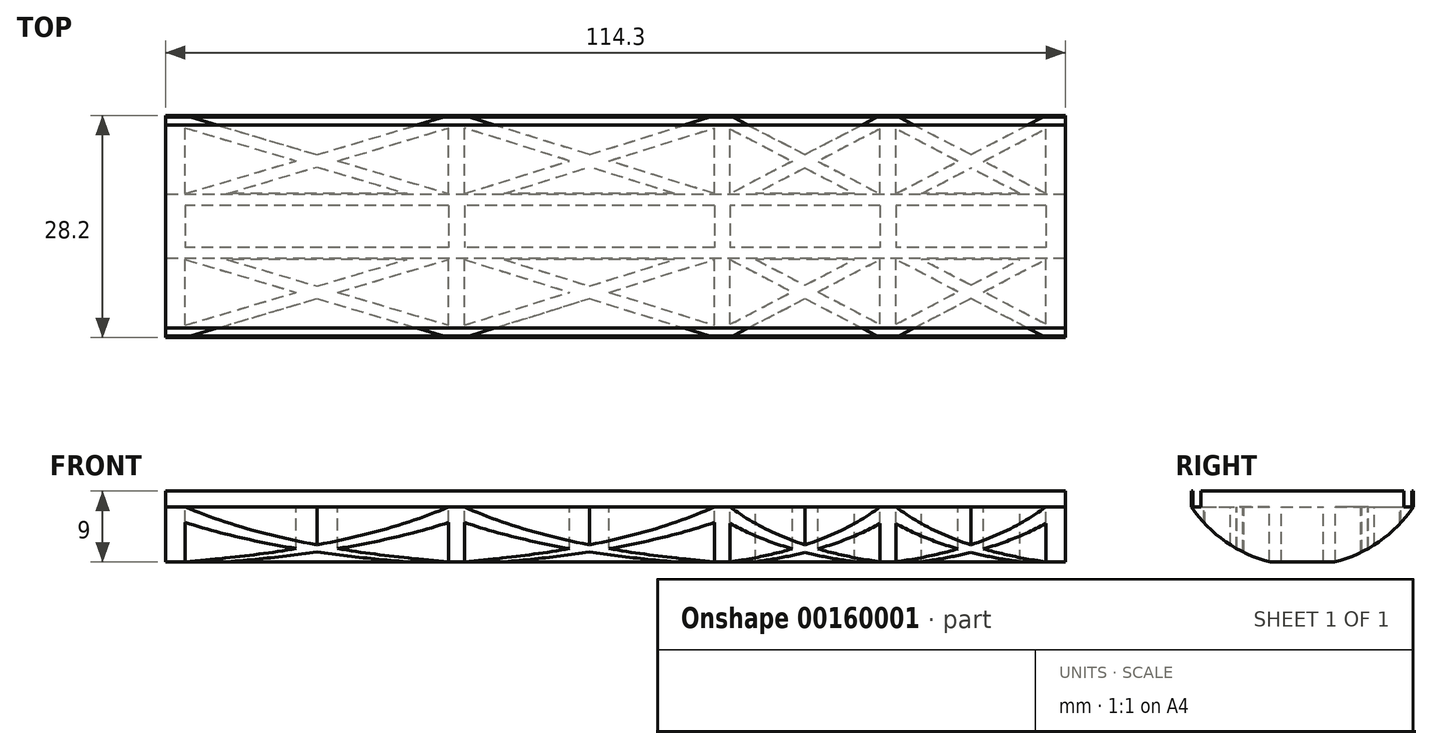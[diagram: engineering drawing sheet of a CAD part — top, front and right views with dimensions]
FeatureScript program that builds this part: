
annotation { "Feature Type Name" : "Feature", "Feature Type Description" : "" }
export const myFeature = defineFeature(function(context is Context, id is Id, definition is map)
    precondition{}
    {
        {
            var Q0;
            Q0=qCreatedBy(makeId("Right.planeOp"),FACE);
            var sketch = newSketch(context, id + "F0", { "sketchPlane" : qUnion([Q0])});
            skArc(sketch, "E0", {"start": v(-14.1, -9.5) * mm, "mid": v(0, -17) * mm, "end": v(14.1, -9.5) * mm});
            skLineSegment(sketch, "E1", {"start": v(-14.1, -9.5) * mm, "end": v(14.1, -9.5) * mm});
            skLineSegment(sketch, "E2", {"start": v(-12.9, -9.5) * mm, "end": v(-12.9, -7.5) * mm});
            skLineSegment(sketch, "E3", {"start": v(-12.9, -7.5) * mm, "end": v(12.9, -7.5) * mm});
            skLineSegment(sketch, "E4", {"start": v(12.9, -7.5) * mm, "end": v(12.9, -9.5) * mm});
            skSolve(sketch);
        }
        {
            var Q0;
            Q0=sQuery(id+"F0.wireOp",EDGE,"E1");
            cPlane(context, id + "F1", {"entities" : qUnion([Q0]), "cplaneType" : CPlaneType.LINE_ANGLE, "offset" : 25.4 * mm, "angle" : 0 * degree, "width" : 152.4 * mm, "height" : 152.4 * mm});
        }
        {
            var Q0;
            Q0 = qSketchRegion(id + "F0", true);
            extrude(context, id + "F2", {"entities" : qUnion([Q0]), "endBound" : BoundingType.SYMMETRIC, "depth" : 114.3 * mm});
        }
        {
            var Q0;
            Q0=qCreatedBy(id+"F1.planeOp",FACE);
            var sketch = newSketch(context, id + "F3", { "sketchPlane" : qUnion([Q0])});
            skLineSegment(sketch, "E5.top", {"start": v(-57.15, 14.1) * mm, "end": v(-54.65, 14.1) * mm});
            skLineSegment(sketch, "E5.left", {"start": v(-57.15, -14.1) * mm, "end": v(-57.15, 14.1) * mm});
            skLineSegment(sketch, "E5.right", {"start": v(57.15, -14.1) * mm, "end": v(57.15, 14.1) * mm});
            skLineSegment(sketch, "E6", {"start": v(-57.15, -14.1) * mm, "end": v(-54.65, -14.1) * mm});
            skLineSegment(sketch, "E7", {"start": v(-54.65, -12.53) * mm, "end": v(-54.65, -4.17) * mm});
            skLineSegment(sketch, "E8", {"start": v(54.65, -12.4) * mm, "end": v(54.65, -4.17) * mm});
            skLineSegment(sketch, "E9", {"start": v(35.6, -12.4) * mm, "end": v(35.6, -4.17) * mm});
            skLineSegment(sketch, "E10", {"start": v(33.6, -12.4) * mm, "end": v(33.6, -4.18) * mm});
            skLineSegment(sketch, "E11", {"start": v(14.55, -12.4) * mm, "end": v(14.55, -4.17) * mm});
            skLineSegment(sketch, "E12", {"start": v(12.55, -12.53) * mm, "end": v(12.55, -4.17) * mm});
            skLineSegment(sketch, "E13", {"start": v(-21.2, -12.53) * mm, "end": v(-21.2, -4.17) * mm});
            skLineSegment(sketch, "E14", {"start": v(-19.2, -12.53) * mm, "end": v(-19.2, -4.17) * mm});
            skLineSegment(sketch, "E15", {"start": v(-54.65, -2.68) * mm, "end": v(-21.2, -2.68) * mm});
            skLineSegment(sketch, "E16", {"start": v(-54.65, 2.68) * mm, "end": v(-21.2, 2.68) * mm});
            skLineSegment(sketch, "E17", {"start": v(-49.38, -4.17) * mm, "end": v(-26.47, -4.17) * mm});
            skLineSegment(sketch, "E18", {"start": v(-49.38, 4.17) * mm, "end": v(-26.47, 4.17) * mm});
            skLineSegment(sketch, "E19", {"start": v(-54.65, -14.1) * mm, "end": v(-37.92, -9.14) * mm});
            skLineSegment(sketch, "E20", {"start": v(-54.65, -4.17) * mm, "end": v(-40.56, -8.35) * mm});
            skLineSegment(sketch, "E21", {"start": v(-19.2, -14.1) * mm, "end": v(-3.32, -9.14) * mm});
            skLineSegment(sketch, "E22", {"start": v(-19.2, -4.18) * mm, "end": v(-5.84, -8.35) * mm});
            skLineSegment(sketch, "E23", {"start": v(14.55, -14.1) * mm, "end": v(24.08, -9.14) * mm});
            skLineSegment(sketch, "E24", {"start": v(14.55, -4.17) * mm, "end": v(22.45, -8.3) * mm});
            skLineSegment(sketch, "E25", {"start": v(35.6, -14.1) * mm, "end": v(45.13, -9.14) * mm});
            skLineSegment(sketch, "E26", {"start": v(54.65, -14.1) * mm, "end": v(45.13, -9.14) * mm});
            skLineSegment(sketch, "E27", {"start": v(-54.65, 14.1) * mm, "end": v(-37.92, 9.14) * mm});
            skLineSegment(sketch, "E28", {"start": v(-19.2, 4.17) * mm, "end": v(-5.84, 8.35) * mm});
            skLineSegment(sketch, "E29", {"start": v(14.55, 14.1) * mm, "end": v(24.08, 9.14) * mm});
            skLineSegment(sketch, "E30", {"start": v(35.6, 4.17) * mm, "end": v(43.5, 8.3) * mm});
            skLineSegment(sketch, "E31", {"start": v(54.65, 4.17) * mm, "end": v(46.75, 8.3) * mm});
            skLineSegment(sketch, "E32", {"start": v(33.6, 14.1) * mm, "end": v(24.08, 9.14) * mm});
            skLineSegment(sketch, "E33", {"start": v(12.55, 4.17) * mm, "end": v(-0.81, 8.35) * mm});
            skLineSegment(sketch, "E34", {"start": v(-54.65, 4.18) * mm, "end": v(-40.56, 8.35) * mm});
            skLineSegment(sketch, "E35.trimOffspring", {"start": v(-21.2, -14.1) * mm, "end": v(-19.2, -14.1) * mm});
            skLineSegment(sketch, "E36.trimOffspring", {"start": v(12.55, -14.1) * mm, "end": v(14.55, -14.1) * mm});
            skLineSegment(sketch, "E37.trimOffspring", {"start": v(33.6, -14.1) * mm, "end": v(35.6, -14.1) * mm});
            skLineSegment(sketch, "E38.trimOffspring", {"start": v(54.65, -14.1) * mm, "end": v(57.15, -14.1) * mm});
            skLineSegment(sketch, "E39.trimOffspring", {"start": v(54.65, 14.1) * mm, "end": v(57.15, 14.1) * mm});
            skLineSegment(sketch, "E40.trimOffspring", {"start": v(33.6, 14.1) * mm, "end": v(35.6, 14.1) * mm});
            skLineSegment(sketch, "E41.trimOffspring", {"start": v(12.55, 14.1) * mm, "end": v(14.55, 14.1) * mm});
            skLineSegment(sketch, "E42.trimOffspring", {"start": v(-21.2, 14.1) * mm, "end": v(-19.2, 14.1) * mm});
            skLineSegment(sketch, "E43.trimOffspring", {"start": v(-14.17, -4.17) * mm, "end": v(7.52, -4.17) * mm});
            skLineSegment(sketch, "E44.trimOffspring", {"start": v(-19.2, -2.68) * mm, "end": v(12.55, -2.68) * mm});
            skLineSegment(sketch, "E45.trimOffspring", {"start": v(-19.2, 2.68) * mm, "end": v(12.55, 2.68) * mm});
            skLineSegment(sketch, "E46.trimOffspring", {"start": v(-14.17, 4.17) * mm, "end": v(7.52, 4.17) * mm});
            skLineSegment(sketch, "E47.trimOffspring", {"start": v(17.8, -4.17) * mm, "end": v(30.35, -4.17) * mm});
            skLineSegment(sketch, "E48.trimOffspring", {"start": v(14.55, -2.68) * mm, "end": v(33.6, -2.68) * mm});
            skLineSegment(sketch, "E49.trimOffspring", {"start": v(38.85, -4.17) * mm, "end": v(51.4, -4.17) * mm});
            skLineSegment(sketch, "E50.trimOffspring", {"start": v(35.6, -2.68) * mm, "end": v(54.65, -2.68) * mm});
            skLineSegment(sketch, "E51.trimOffspring", {"start": v(35.6, 2.68) * mm, "end": v(54.65, 2.68) * mm});
            skLineSegment(sketch, "E52.trimOffspring", {"start": v(38.85, 4.17) * mm, "end": v(51.4, 4.17) * mm});
            skLineSegment(sketch, "E53.trimOffspring", {"start": v(-54.65, 4.18) * mm, "end": v(-54.65, 12.53) * mm});
            skLineSegment(sketch, "E54.trimOffspring", {"start": v(-54.65, -2.68) * mm, "end": v(-54.65, 2.67) * mm});
            skLineSegment(sketch, "E55.trimOffspring", {"start": v(-21.2, 4.18) * mm, "end": v(-21.2, 12.53) * mm});
            skLineSegment(sketch, "E56.trimOffspring", {"start": v(-19.2, 4.17) * mm, "end": v(-19.2, 12.53) * mm});
            skLineSegment(sketch, "E57.trimOffspring", {"start": v(-19.2, -2.68) * mm, "end": v(-19.2, 2.67) * mm});
            skLineSegment(sketch, "E58.trimOffspring", {"start": v(-21.2, -2.67) * mm, "end": v(-21.2, 2.67) * mm});
            skLineSegment(sketch, "E59.trimOffspring", {"start": v(12.55, -2.68) * mm, "end": v(12.55, 2.68) * mm});
            skLineSegment(sketch, "E60.trimOffspring", {"start": v(14.55, -2.68) * mm, "end": v(14.55, 2.68) * mm});
            skLineSegment(sketch, "E61.trimOffspring", {"start": v(14.55, 4.17) * mm, "end": v(14.55, 12.4) * mm});
            skLineSegment(sketch, "E62.trimOffspring", {"start": v(14.55, 2.68) * mm, "end": v(33.6, 2.68) * mm});
            skLineSegment(sketch, "E63.trimOffspring", {"start": v(17.8, 4.17) * mm, "end": v(30.35, 4.17) * mm});
            skLineSegment(sketch, "E64.trimOffspring", {"start": v(12.55, 4.17) * mm, "end": v(12.55, 12.53) * mm});
            skLineSegment(sketch, "E65.trimOffspring", {"start": v(33.6, 4.17) * mm, "end": v(33.6, 12.4) * mm});
            skLineSegment(sketch, "E66.trimOffspring", {"start": v(35.6, 4.17) * mm, "end": v(35.6, 12.4) * mm});
            skLineSegment(sketch, "E67.trimOffspring", {"start": v(54.65, 4.17) * mm, "end": v(54.65, 12.4) * mm});
            skLineSegment(sketch, "E68.trimOffspring", {"start": v(54.65, -2.67) * mm, "end": v(54.65, 2.68) * mm});
            skLineSegment(sketch, "E69.0", {"start": v(-49.38, 4.18) * mm, "end": v(-37.93, 7.57) * mm});
            skLineSegment(sketch, "E70.0", {"start": v(-54.65, 12.53) * mm, "end": v(-40.56, 8.35) * mm});
            skLineSegment(sketch, "E71.0", {"start": v(-14.17, 4.18) * mm, "end": v(-3.33, 7.56) * mm});
            skLineSegment(sketch, "E72.0", {"start": v(7.52, 4.17) * mm, "end": v(-3.33, 7.56) * mm});
            skLineSegment(sketch, "E73.0", {"start": v(33.6, 12.4) * mm, "end": v(25.7, 8.3) * mm});
            skLineSegment(sketch, "E74.0", {"start": v(14.55, 12.4) * mm, "end": v(22.45, 8.3) * mm});
            skLineSegment(sketch, "E75.0", {"start": v(38.85, 4.17) * mm, "end": v(45.13, 7.44) * mm});
            skLineSegment(sketch, "E76.0", {"start": v(51.4, 4.17) * mm, "end": v(45.13, 7.44) * mm});
            skLineSegment(sketch, "E77.0", {"start": v(54.65, -12.4) * mm, "end": v(46.75, -8.3) * mm});
            skLineSegment(sketch, "E78.0", {"start": v(35.6, -12.4) * mm, "end": v(43.5, -8.3) * mm});
            skLineSegment(sketch, "E79.0", {"start": v(17.8, -4.17) * mm, "end": v(24.08, -7.44) * mm});
            skLineSegment(sketch, "E80.0", {"start": v(14.55, -12.4) * mm, "end": v(22.45, -8.3) * mm});
            skLineSegment(sketch, "E81.0", {"start": v(-14.17, -4.18) * mm, "end": v(-3.32, -7.56) * mm});
            skLineSegment(sketch, "E82.0", {"start": v(-19.2, -12.53) * mm, "end": v(-5.84, -8.35) * mm});
            skLineSegment(sketch, "E83.0", {"start": v(-54.65, -12.53) * mm, "end": v(-40.56, -8.35) * mm});
            skLineSegment(sketch, "E84.0", {"start": v(-49.38, -4.17) * mm, "end": v(-37.92, -7.57) * mm});
            skLineSegment(sketch, "E85.trimOffspring", {"start": v(-35.29, -8.35) * mm, "end": v(-21.2, -4.18) * mm});
            skLineSegment(sketch, "E86.trimOffspring", {"start": v(-35.29, -8.35) * mm, "end": v(-21.2, -12.53) * mm});
            skLineSegment(sketch, "E87.trimOffspring", {"start": v(-37.92, -7.57) * mm, "end": v(-26.47, -4.17) * mm});
            skLineSegment(sketch, "E88.trimOffspring", {"start": v(-37.92, -9.14) * mm, "end": v(-21.2, -14.1) * mm});
            skLineSegment(sketch, "E89.trimOffspring", {"start": v(-0.81, -8.35) * mm, "end": v(12.55, -4.18) * mm});
            skLineSegment(sketch, "E90.trimOffspring", {"start": v(-3.32, -9.14) * mm, "end": v(12.55, -14.1) * mm});
            skLineSegment(sketch, "E91.trimOffspring", {"start": v(-0.81, -8.35) * mm, "end": v(12.55, -12.53) * mm});
            skLineSegment(sketch, "E92.trimOffspring", {"start": v(-3.33, -7.56) * mm, "end": v(7.52, -4.17) * mm});
            skLineSegment(sketch, "E93.trimOffspring", {"start": v(24.08, -9.14) * mm, "end": v(33.6, -14.1) * mm});
            skLineSegment(sketch, "E94.trimOffspring", {"start": v(25.7, -8.3) * mm, "end": v(33.6, -4.18) * mm});
            skLineSegment(sketch, "E95.trimOffspring", {"start": v(25.7, -8.3) * mm, "end": v(33.6, -12.4) * mm});
            skLineSegment(sketch, "E96.trimOffspring", {"start": v(24.08, -7.44) * mm, "end": v(30.35, -4.17) * mm});
            skLineSegment(sketch, "E97.trimOffspring", {"start": v(43.5, -8.3) * mm, "end": v(35.6, -4.17) * mm});
            skLineSegment(sketch, "E98.trimOffspring", {"start": v(46.75, -8.3) * mm, "end": v(54.65, -4.17) * mm});
            skLineSegment(sketch, "E99.trimOffspring", {"start": v(45.13, -7.44) * mm, "end": v(38.85, -4.17) * mm});
            skLineSegment(sketch, "E100.trimOffspring", {"start": v(45.13, -7.44) * mm, "end": v(51.4, -4.17) * mm});
            skLineSegment(sketch, "E101.trimOffspring", {"start": v(35.6, -2.68) * mm, "end": v(35.6, 2.68) * mm});
            skLineSegment(sketch, "E102.trimOffspring", {"start": v(33.6, -2.68) * mm, "end": v(33.6, 2.68) * mm});
            skLineSegment(sketch, "E103.trimOffspring", {"start": v(46.75, 8.3) * mm, "end": v(54.65, 12.4) * mm});
            skLineSegment(sketch, "E104.trimOffspring", {"start": v(43.5, 8.3) * mm, "end": v(35.6, 12.4) * mm});
            skLineSegment(sketch, "E105.trimOffspring", {"start": v(45.13, 9.14) * mm, "end": v(35.6, 14.1) * mm});
            skLineSegment(sketch, "E106.trimOffspring", {"start": v(45.13, 9.14) * mm, "end": v(54.65, 14.1) * mm});
            skLineSegment(sketch, "E107.trimOffspring", {"start": v(24.07, 7.44) * mm, "end": v(17.8, 4.17) * mm});
            skLineSegment(sketch, "E108.trimOffspring", {"start": v(24.07, 7.44) * mm, "end": v(30.35, 4.18) * mm});
            skLineSegment(sketch, "E109.trimOffspring", {"start": v(22.45, 8.3) * mm, "end": v(14.55, 4.17) * mm});
            skLineSegment(sketch, "E110.trimOffspring", {"start": v(25.7, 8.3) * mm, "end": v(33.6, 4.18) * mm});
            skLineSegment(sketch, "E111.trimOffspring", {"start": v(-0.81, 8.35) * mm, "end": v(12.55, 12.53) * mm});
            skLineSegment(sketch, "E112.trimOffspring", {"start": v(-3.32, 9.14) * mm, "end": v(-19.2, 14.1) * mm});
            skLineSegment(sketch, "E113.trimOffspring", {"start": v(-3.33, 9.14) * mm, "end": v(12.55, 14.1) * mm});
            skLineSegment(sketch, "E114.trimOffspring", {"start": v(-5.84, 8.35) * mm, "end": v(-19.2, 12.53) * mm});
            skLineSegment(sketch, "E115.trimOffspring", {"start": v(-35.29, 8.35) * mm, "end": v(-21.2, 12.53) * mm});
            skLineSegment(sketch, "E116.trimOffspring", {"start": v(-35.29, 8.35) * mm, "end": v(-21.2, 4.17) * mm});
            skLineSegment(sketch, "E117.trimOffspring", {"start": v(-37.93, 7.57) * mm, "end": v(-26.47, 4.17) * mm});
            skLineSegment(sketch, "E118.trimOffspring", {"start": v(-37.92, 9.14) * mm, "end": v(-21.2, 14.1) * mm});
            skSolve(sketch);
        }
        {
            var Q0;
            Q0 = qSketchRegion(id + "F3", true);
            extrude(context, id + "F4", {"entities" : qUnion([Q0]), "operationType" : NewBodyOperationType.INTERSECT, "oppositeDirection" : true, "depth" : 25.4 * mm});
        }
        {
            var Q0;
            Q0=makeQuery(id+"F2.opExtrude","CAP_FACE",FACE,{"disambiguationData":[OSD([sQuery(id+"F0.wireOp",EDGE,"E0"),sQuery(id+"F0.wireOp",EDGE,"E1"),sQuery(id+"F0.wireOp",EDGE,"E2"),sQuery(id+"F0.wireOp",EDGE,"E3"),sQuery(id+"F0.wireOp",EDGE,"E4")])],"isStart":false});
            var sketch = newSketch(context, id + "F5", { "sketchPlane" : qUnion([Q0])});
            skLineSegment(sketch, "E119", {"start": v(-12.9, -9.5) * mm, "end": v(-12.9, -7.5) * mm});
            skLineSegment(sketch, "E120", {"start": v(-12.9, -7.5) * mm, "end": v(12.9, -7.5) * mm});
            skLineSegment(sketch, "E121", {"start": v(12.9, -7.5) * mm, "end": v(12.9, -9.5) * mm});
            skLineSegment(sketch, "E122", {"start": v(-12.9, -9.5) * mm, "end": v(12.9, -9.5) * mm});
            skSolve(sketch);
        }
        {
            var Q0;
            Q0 = qSketchRegion(id + "F5", true);
            extrude(context, id + "F6", {"entities" : qUnion([Q0]), "operationType" : NewBodyOperationType.ADD, "oppositeDirection" : true, "depth" : 114.3 * mm});
        }
        {
            var Q0;
            Q0=makeQuery(id+"F6.boolean.opBoolean","MERGE",FACE,{"derivedFrom":[makeQuery(id+"F2.opExtrude","CAP_FACE",FACE,{"disambiguationData":[OSD([sQuery(id+"F0.wireOp",EDGE,"E0"),sQuery(id+"F0.wireOp",EDGE,"E1"),sQuery(id+"F0.wireOp",EDGE,"E2"),sQuery(id+"F0.wireOp",EDGE,"E3"),sQuery(id+"F0.wireOp",EDGE,"E4")])],"isStart":false}),makeQuery(id+"F6.opExtrude","CAP_FACE",FACE,{"disambiguationData":[OSD([sQuery(id+"F5.wireOp",EDGE,"E119"),sQuery(id+"F5.wireOp",EDGE,"E120"),sQuery(id+"F5.wireOp",EDGE,"E121"),sQuery(id+"F5.wireOp",EDGE,"E122")])],"isStart":true})]});
            var sketch = newSketch(context, id + "F7", { "sketchPlane" : qUnion([Q0])});
            skLineSegment(sketch, "E123.bottom", {"start": v(11.06, -21.2) * mm, "end": v(-13.89, -21.2) * mm});
            skLineSegment(sketch, "E123.top", {"start": v(11.06, -16.5) * mm, "end": v(-13.89, -16.5) * mm});
            skLineSegment(sketch, "E123.left", {"start": v(11.06, -21.2) * mm, "end": v(11.06, -16.5) * mm});
            skLineSegment(sketch, "E123.right", {"start": v(-13.89, -21.2) * mm, "end": v(-13.89, -16.5) * mm});
            skSolve(sketch);
        }
        {
            var Q0;
            Q0 = qSketchRegion(id + "F7", true);
            extrude(context, id + "F8", {"entities" : qUnion([Q0]), "operationType" : NewBodyOperationType.REMOVE, "oppositeDirection" : true, "depth" : 114.3 * mm});
        }
        {
            var Q0;
            Q0=makeQuery(id+"F6.boolean.opBoolean","MERGE",FACE,{"derivedFrom":[makeQuery(id+"F2.opExtrude","CAP_FACE",FACE,{"disambiguationData":[OSD([sQuery(id+"F0.wireOp",EDGE,"E0"),sQuery(id+"F0.wireOp",EDGE,"E1"),sQuery(id+"F0.wireOp",EDGE,"E2"),sQuery(id+"F0.wireOp",EDGE,"E3"),sQuery(id+"F0.wireOp",EDGE,"E4")])],"isStart":false}),makeQuery(id+"F6.opExtrude","CAP_FACE",FACE,{"disambiguationData":[OSD([sQuery(id+"F5.wireOp",EDGE,"E119"),sQuery(id+"F5.wireOp",EDGE,"E120"),sQuery(id+"F5.wireOp",EDGE,"E121"),sQuery(id+"F5.wireOp",EDGE,"E122")])],"isStart":true})]});
            var sketch = newSketch(context, id + "F9", { "sketchPlane" : qUnion([Q0])});
            skLineSegment(sketch, "E124.bottom", {"start": v(-14.1, -9.5) * mm, "end": v(-13.9, -9.5) * mm});
            skLineSegment(sketch, "E124.top", {"start": v(-14.1, -7.5) * mm, "end": v(-13.9, -7.5) * mm});
            skLineSegment(sketch, "E124.left", {"start": v(-14.1, -9.5) * mm, "end": v(-14.1, -7.5) * mm});
            skLineSegment(sketch, "E124.right", {"start": v(-13.9, -9.5) * mm, "end": v(-13.9, -7.5) * mm});
            skLineSegment(sketch, "E125.bottom", {"start": v(14.1, -9.5) * mm, "end": v(13.9, -9.5) * mm});
            skLineSegment(sketch, "E125.top", {"start": v(14.1, -7.5) * mm, "end": v(13.9, -7.5) * mm});
            skLineSegment(sketch, "E125.left", {"start": v(14.1, -9.5) * mm, "end": v(14.1, -7.5) * mm});
            skLineSegment(sketch, "E125.right", {"start": v(13.9, -9.5) * mm, "end": v(13.9, -7.5) * mm});
            skSolve(sketch);
        }
        {
            var Q0;
            Q0 = qSketchRegion(id + "F9", true);
            extrude(context, id + "F10", {"entities" : qUnion([Q0]), "operationType" : NewBodyOperationType.ADD, "oppositeDirection" : true, "depth" : 114.3 * mm});
        }
    });
